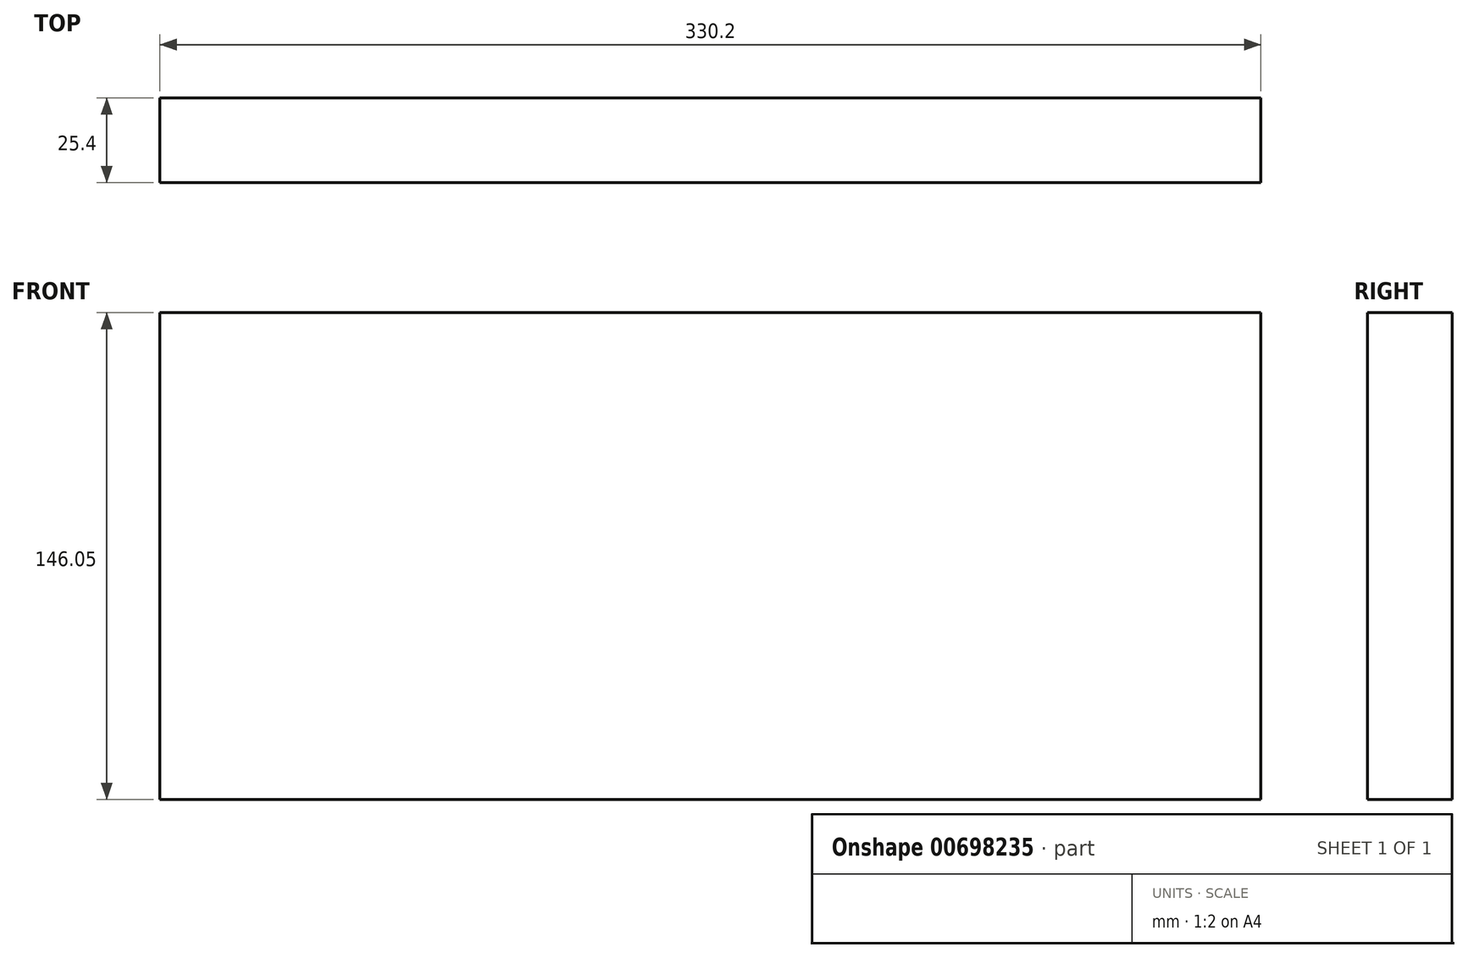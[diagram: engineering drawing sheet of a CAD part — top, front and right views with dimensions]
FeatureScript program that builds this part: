
annotation { "Feature Type Name" : "Feature", "Feature Type Description" : "" }
export const myFeature = defineFeature(function(context is Context, id is Id, definition is map)
    precondition{}
    {
        {
            var Q0;
            Q0=qCreatedBy(makeId("Front.planeOp"),FACE);
            var sketch = newSketch(context, id + "F0", { "sketchPlane" : qUnion([Q0])});
            skLineSegment(sketch, "E0.bottom", {"start": v(-148.3, 60.4) * mm, "end": v(181.9, 60.4) * mm});
            skLineSegment(sketch, "E0.top", {"start": v(-148.3, -85.65) * mm, "end": v(181.9, -85.65) * mm});
            skLineSegment(sketch, "E0.left", {"start": v(-148.3, 60.4) * mm, "end": v(-148.3, -85.65) * mm});
            skLineSegment(sketch, "E0.right", {"start": v(181.9, 60.4) * mm, "end": v(181.9, -85.65) * mm});
            skSolve(sketch);
        }
        {
            var Q0;
            Q0=makeQuery(id+"F0.imprint","IMPRINT",FACE,{"disambiguationData":[TD([[makeQuery(id+"F0.imprint","IMPRINT",EDGE,{"derivedFrom":sQuery(id+"F0.wireOp",EDGE,"E0.bottom")}),-1.0]])]});
            extrude(context, id + "F1", {"entities" : qUnion([Q0]), "depth" : 25.4 * mm, "offsetDistance" : 25.4 * mm});
        }
    });
